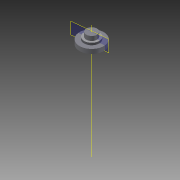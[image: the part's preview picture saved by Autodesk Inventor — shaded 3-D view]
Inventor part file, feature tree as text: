
AUTODESK INVENTOR PART (.ipt)
format: ipt  version: 2012 (Build 160160000, 160)  size: 1,804,800 bytes
history: native  units: mm
features: sketch x7, other x4, extrude x4, projected_geometry x2, plane x1
ambient origin geometry x8: Origin, YZ Plane, XZ Plane, XY Plane, X Axis, Y Axis, Z Axis, Center Point
bodies: Solid1 (feature_tree)
feature tree (18):
  other  "Gear2_LargeAndSmall.iam"
  other  "Spur Gear2:1"
  other  "Spur Gear1:1"
  sketch  "Sketch2"  dims[d0=10.0mm d1=3.3mm]
  sketch  "Sketch3"  dims[d2=10.0mm d3=0.0mm d4=22.5mm]
  other  "Work Axis1"
  extrude  "Extrusion1"  Depth=3.3mm
  sketch  "Sketch5"  dims[d8=10.0mm d9=0.0mm d11=10.0mm d12=0.0mm]
  plane  "Work Plane1"
  extrude  "Extrusion2"  Depth=22.5mm
  extrude  "Extrusion3"  Depth=15.909903mm
  extrude  "Extrusion4"  Depth=10.0mm TaperAngle=0.0deg
  projected_geometry  "Projected Loop1"
  projected_geometry  "Projected Loop2"
  sketch  "Sketch4"  dims[d5=10.0mm d6=0.0mm d7=15.909903mm]
  sketch  "Sketch6"
  sketch  "Sketch7"
  sketch  "Sketch8"
